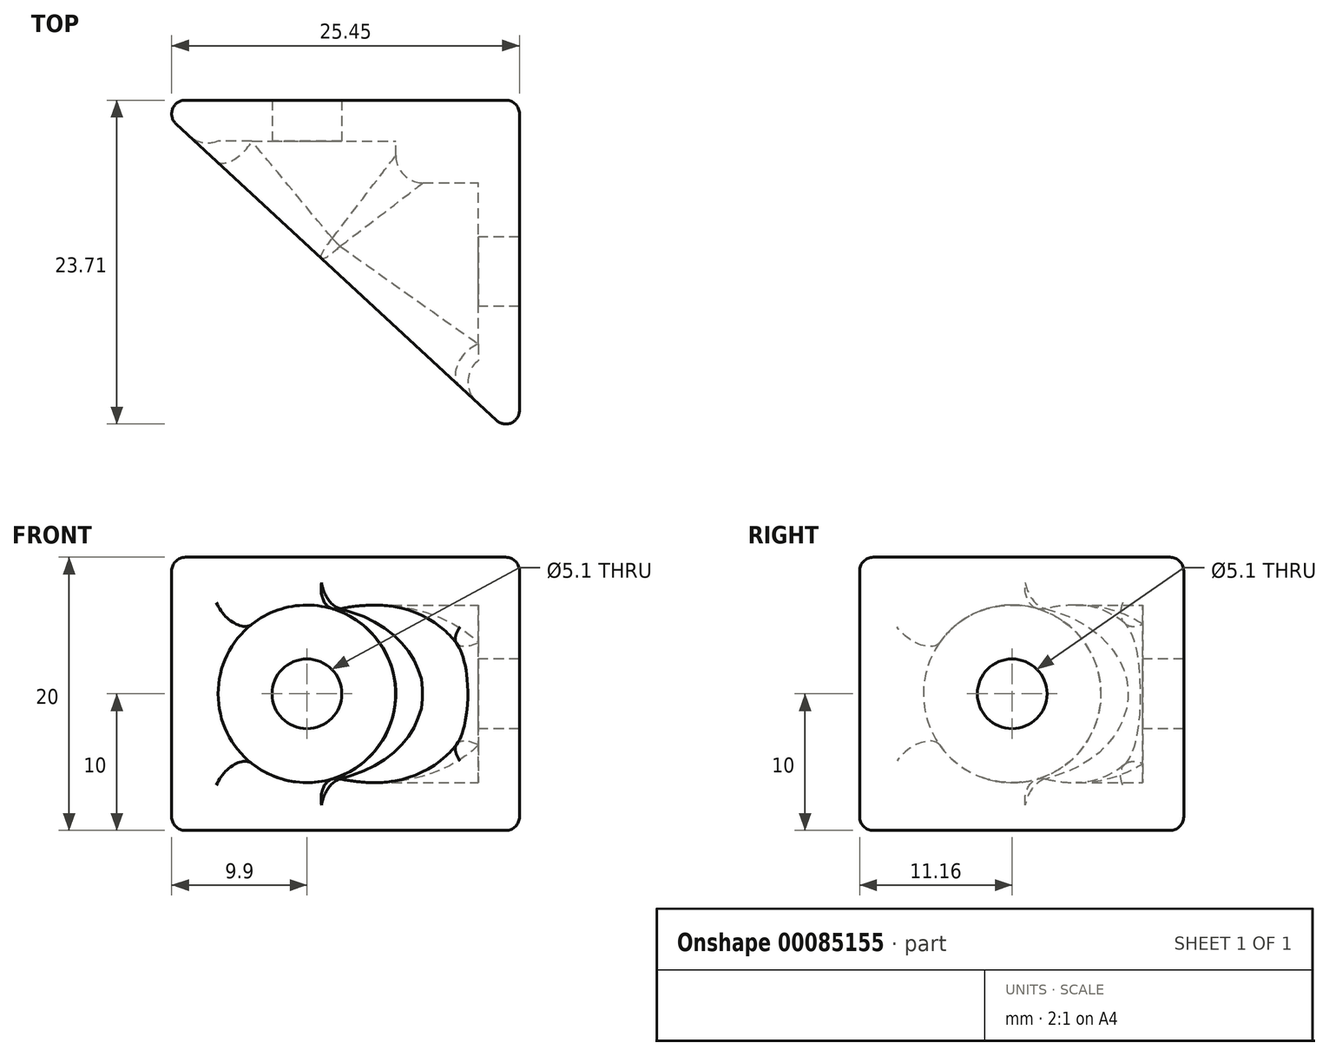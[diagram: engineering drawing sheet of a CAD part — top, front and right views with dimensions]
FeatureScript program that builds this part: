
annotation { "Feature Type Name" : "Feature", "Feature Type Description" : "" }
export const myFeature = defineFeature(function(context is Context, id is Id, definition is map)
    precondition{}
    {
        {
            assignVariable(context, id + "F0", {"name" : "Thickness", "anyValue" : 3});
        }
        {
            var Q0;
            Q0=qCreatedBy(makeId("Front.planeOp"),FACE);
            var sketch = newSketch(context, id + "F1", { "sketchPlane" : qUnion([Q0])});
            skLineSegment(sketch, "E0.bottom", {"start": v(0, 20) * mm, "end": v(-27, 20) * mm});
            skLineSegment(sketch, "E0.top", {"start": v(0, 0) * mm, "end": v(-27, 0) * mm});
            skLineSegment(sketch, "E0.left", {"start": v(0, 20) * mm, "end": v(0, 0) * mm});
            skLineSegment(sketch, "E0.right", {"start": v(-27, 20) * mm, "end": v(-27, 0) * mm});
            skSolve(sketch);
        }
        {
            var Q0;
            Q0=qCreatedBy(makeId("Right.planeOp"),FACE);
            var sketch = newSketch(context, id + "F2", { "sketchPlane" : qUnion([Q0])});
            skLineSegment(sketch, "E1.bottom", {"start": v(0, 0) * mm, "end": v(-25, 0) * mm});
            skLineSegment(sketch, "E1.top", {"start": v(0, 20) * mm, "end": v(-25, 20) * mm});
            skLineSegment(sketch, "E1.left", {"start": v(0, 0) * mm, "end": v(0, 20) * mm});
            skLineSegment(sketch, "E1.right", {"start": v(-25, 0) * mm, "end": v(-25, 20) * mm});
            skSolve(sketch);
        }
        {
            var Q0;
            Q0=makeQuery(id+"F1.imprint","IMPRINT",FACE,{"disambiguationData":[TD([[makeQuery(id+"F1.imprint","IMPRINT",EDGE,{"derivedFrom":sQuery(id+"F1.wireOp",EDGE,"E0.bottom")}),1.0]])]});
            var Q1;
            Q1=makeQuery(id+"F2.imprint","IMPRINT",FACE,{"disambiguationData":[TD([[makeQuery(id+"F2.imprint","IMPRINT",EDGE,{"derivedFrom":sQuery(id+"F2.wireOp",EDGE,"E1.bottom")}),-1.0]])]});
            var Q2;
            Q2=sQuery(id+"F1.wireOp",VERTEX,"E0.right.start");
            var Q3;
            Q3=sQuery(id+"F2.wireOp",VERTEX,"E1.right.end");
            loft(context, id + "F3", {"sheetProfilesArray" : [{ "sheetProfileEntities" : qUnion([Q0]) }, { "sheetProfileEntities" : qUnion([Q1]) }], "matchConnections" : true, "connections" : [{ "connectionEntities" : qUnion([Q2, Q3]), "connectionEdgeQueries" : qUnion([]), "connectionEdgeParameters" : [] }]});
        }
        {
            var Q0;
            Q0=qCreatedBy(makeId("Front.planeOp"),FACE);
            cPlane(context, id + "F4", {"entities" : qUnion([Q0]), "cplaneType" : CPlaneType.OFFSET, "offset" : (getVariable(context, 'Thickness')) * mm, "width" : 150 * mm, "height" : 150 * mm});
        }
        {
            var Q0;
            Q0=qCreatedBy(id+"F4.planeOp",FACE);
            var sketch = newSketch(context, id + "F5", { "sketchPlane" : qUnion([Q0])});
            skCircle(sketch, "E2", {"center": v(-15.55, 10) * mm, "radius": 6.5 * mm});
            skCircle(sketch, "E3", {"center": v(-15.55, 10) * mm, "radius": 2.55 * mm});
            skSolve(sketch);
        }
        {
            var Q0;
            Q0 = qSketchRegion(id + "F5", true);
            extrude(context, id + "F6", {"entities" : qUnion([Q0]), "operationType" : NewBodyOperationType.REMOVE, "depth" : 25 * mm});
        }
        {
            var Q0;
            Q0=makeQuery(id+"F5.imprint","IMPRINT",FACE,{"disambiguationData":[TD([[makeQuery(id+"F5.imprint","IMPRINT",EDGE,{"derivedFrom":sQuery(id+"F5.wireOp",EDGE,"E3")}),1.0]])]});
            extrude(context, id + "F7", {"entities" : qUnion([Q0]), "operationType" : NewBodyOperationType.REMOVE, "oppositeDirection" : true, "depth" : 25 * mm, "hasSecondDirection" : true, "secondDirectionOppositeDirection" : false, "secondDirectionDepth" : 25 * mm});
        }
        {
            var Q0;
            Q0=qCreatedBy(makeId("Right.planeOp"),FACE);
            cPlane(context, id + "F8", {"entities" : qUnion([Q0]), "cplaneType" : CPlaneType.OFFSET, "offset" : (getVariable(context, 'Thickness')) * mm, "oppositeDirection" : true, "width" : 150 * mm, "height" : 150 * mm});
        }
        {
            var Q0;
            Q0=qCreatedBy(id+"F8.planeOp",FACE);
            var sketch = newSketch(context, id + "F9", { "sketchPlane" : qUnion([Q0])});
            skCircle(sketch, "E4", {"center": v(-12.55, 10) * mm, "radius": 6.5 * mm});
            skCircle(sketch, "E5", {"center": v(-12.55, 10) * mm, "radius": 2.55 * mm});
            skSolve(sketch);
        }
        {
            var Q0;
            Q0=makeQuery(id+"F9.imprint","IMPRINT",FACE,{"disambiguationData":[TD([[makeQuery(id+"F9.imprint","IMPRINT",EDGE,{"derivedFrom":sQuery(id+"F9.wireOp",EDGE,"E4")}),1.0]])]});
            var Q1;
            Q1=makeQuery(id+"F9.imprint","IMPRINT",FACE,{"disambiguationData":[TD([[makeQuery(id+"F9.imprint","IMPRINT",EDGE,{"derivedFrom":sQuery(id+"F9.wireOp",EDGE,"E5")}),1.0]])]});
            extrude(context, id + "F10", {"entities" : qUnion([Q0, Q1]), "operationType" : NewBodyOperationType.REMOVE, "oppositeDirection" : true, "depth" : 25 * mm});
        }
        {
            var Q0;
            Q0=makeQuery(id+"F9.imprint","IMPRINT",FACE,{"disambiguationData":[TD([[makeQuery(id+"F9.imprint","IMPRINT",EDGE,{"derivedFrom":sQuery(id+"F9.wireOp",EDGE,"E5")}),1.0]])]});
            extrude(context, id + "F11", {"entities" : qUnion([Q0]), "operationType" : NewBodyOperationType.REMOVE, "depth" : 25 * mm});
        }
        {
            var Q0;
            Q0=makeQuery(id+"F3.opLoft","SWEPT_EDGE",EDGE,{"disambiguationData":[OSD([sQuery(id+"F1.wireOp",EDGE,"E0.bottom"),sQuery(id+"F1.wireOp",EDGE,"E0.right"),sQuery(id+"F2.wireOp",EDGE,"E1.top"),sQuery(id+"F2.wireOp",EDGE,"E1.right")])]});
            var Q1;
            Q1=makeQuery(id+"F3.opLoft","SWEPT_EDGE",EDGE,{"disambiguationData":[OSD([sQuery(id+"F1.wireOp",EDGE,"E0.top"),sQuery(id+"F1.wireOp",EDGE,"E0.right"),sQuery(id+"F2.wireOp",EDGE,"E1.bottom"),sQuery(id+"F2.wireOp",EDGE,"E1.right")])]});
            var Q2;
            Q2=makeQuery(id+"F3.opLoft","MID_CAP_EDGE",EDGE,{"disambiguationData":[OSD([sQuery(id+"F1.wireOp",EDGE,"E0.bottom"),sQuery(id+"F1.wireOp",EDGE,"E0.top"),sQuery(id+"F1.wireOp",EDGE,"E0.right")])],"capPos":0.0});
            var Q3;
            Q3=makeQuery(id+"F3.opLoft","MID_CAP_EDGE",EDGE,{"disambiguationData":[OSD([sQuery(id+"F2.wireOp",EDGE,"E1.bottom"),sQuery(id+"F2.wireOp",EDGE,"E1.top"),sQuery(id+"F2.wireOp",EDGE,"E1.right")])],"capPos":1.0});
            var Q4;
            Q4=makeQuery(id+"F3.opLoft","MID_CAP_EDGE",EDGE,{"disambiguationData":[OSD([sQuery(id+"F2.wireOp",EDGE,"E1.bottom"),sQuery(id+"F2.wireOp",EDGE,"E1.left"),sQuery(id+"F2.wireOp",EDGE,"E1.right")])],"capPos":1.0});
            var Q5;
            Q5=makeQuery(id+"F3.opLoft","MID_CAP_EDGE",EDGE,{"disambiguationData":[OSD([sQuery(id+"F1.wireOp",EDGE,"E0.top"),sQuery(id+"F1.wireOp",EDGE,"E0.left"),sQuery(id+"F1.wireOp",EDGE,"E0.right")])],"capPos":0.0});
            var Q6;
            Q6=makeQuery(id+"F3.opLoft","MID_CAP_EDGE",EDGE,{"disambiguationData":[OSD([sQuery(id+"F2.wireOp",EDGE,"E1.top"),sQuery(id+"F2.wireOp",EDGE,"E1.left"),sQuery(id+"F2.wireOp",EDGE,"E1.right")])],"capPos":1.0});
            var Q7;
            Q7=makeQuery(id+"F3.opLoft","MID_CAP_EDGE",EDGE,{"disambiguationData":[OSD([sQuery(id+"F1.wireOp",EDGE,"E0.bottom"),sQuery(id+"F1.wireOp",EDGE,"E0.left"),sQuery(id+"F1.wireOp",EDGE,"E0.right")])],"capPos":0.0});
            var Q8;
            Q8=makeQuery(id+"F3.opLoft","CAP_EDGE",EDGE,{"disambiguationData":[OSD([sQuery(id+"F1.wireOp",EDGE,"E0.left"),sQuery(id+"F2.wireOp",EDGE,"E1.left")])],"isStart":false});
            fillet(context, id + "F12", {"entities" : qUnion([Q0, Q1, Q2, Q3, Q4, Q5, Q6, Q7, Q8]), "radius" : 1 * mm, "tangentPropagation" : true, "allowEdgeOverflow" : false});
        }
        {
            var Q0;
            Q0=makeQuery(id+"F6.boolean.opBoolean","INTERSECT",EDGE,{"derivedFrom":[makeQuery(id+"F3.opLoft","SWEPT_FACE",FACE,{"disambiguationData":[OSD([sQuery(id+"F1.wireOp",EDGE,"E0.bottom"),sQuery(id+"F1.wireOp",EDGE,"E0.top"),sQuery(id+"F1.wireOp",EDGE,"E0.right"),sQuery(id+"F2.wireOp",EDGE,"E1.bottom"),sQuery(id+"F2.wireOp",EDGE,"E1.top"),sQuery(id+"F2.wireOp",EDGE,"E1.right")])]}),makeQuery(id+"F6.opExtrude","SWEPT_FACE",FACE,{"disambiguationData":[OSD([sQuery(id+"F5.wireOp",EDGE,"E2")])]})]});
            var Q1;
            {var subQ0=sQuery(id+"F2.wireOp",EDGE,"E1.bottom");var subQ2=sQuery(id+"F2.wireOp",EDGE,"E1.top");var subQ3=sQuery(id+"F2.wireOp",EDGE,"E1.right");var subQ4=sQuery(id+"F1.wireOp",EDGE,"E0.bottom");var subQ5=sQuery(id+"F1.wireOp",EDGE,"E0.top");var subQ7=sQuery(id+"F1.wireOp",EDGE,"E0.right");Q1=makeQuery(id+"F10.boolean.opBoolean","INTERSECT",EDGE,{"derivedFrom":[makeQuery(id+"F6.boolean.opBoolean","SPLIT",FACE,{"disambiguationData":[TD([makeQuery(id+"F6.opExtrude","SWEPT_FACE",FACE,{"disambiguationData":[OSD([sQuery(id+"F5.wireOp",EDGE,"E2")])]})])],"derivedFrom":makeQuery(id+"F3.opLoft","SWEPT_FACE",FACE,{"disambiguationData":[OSD([subQ4,subQ5,subQ7,subQ0,subQ2,subQ3])]})}),makeQuery(id+"F10.opExtrude","SWEPT_FACE",FACE,{"disambiguationData":[OSD([sQuery(id+"F9.wireOp",EDGE,"E4")])]})]});}
            var Q2;
            Q2=makeQuery(id+"F10.boolean.opBoolean","INTERSECT",EDGE,{"derivedFrom":[makeQuery(id+"F6.boolean.opBoolean","COPY",FACE,{"derivedFrom":makeQuery(id+"F6.opExtrude","SWEPT_FACE",FACE,{"disambiguationData":[OSD([sQuery(id+"F5.wireOp",EDGE,"E2")])]})}),makeQuery(id+"F10.opExtrude","SWEPT_FACE",FACE,{"disambiguationData":[OSD([sQuery(id+"F9.wireOp",EDGE,"E4")])]})]});
            fillet(context, id + "F13", {"entities" : qUnion([Q0, Q1, Q2]), "radius" : 2 * mm, "tangentPropagation" : true, "allowEdgeOverflow" : false});
        }
    });
